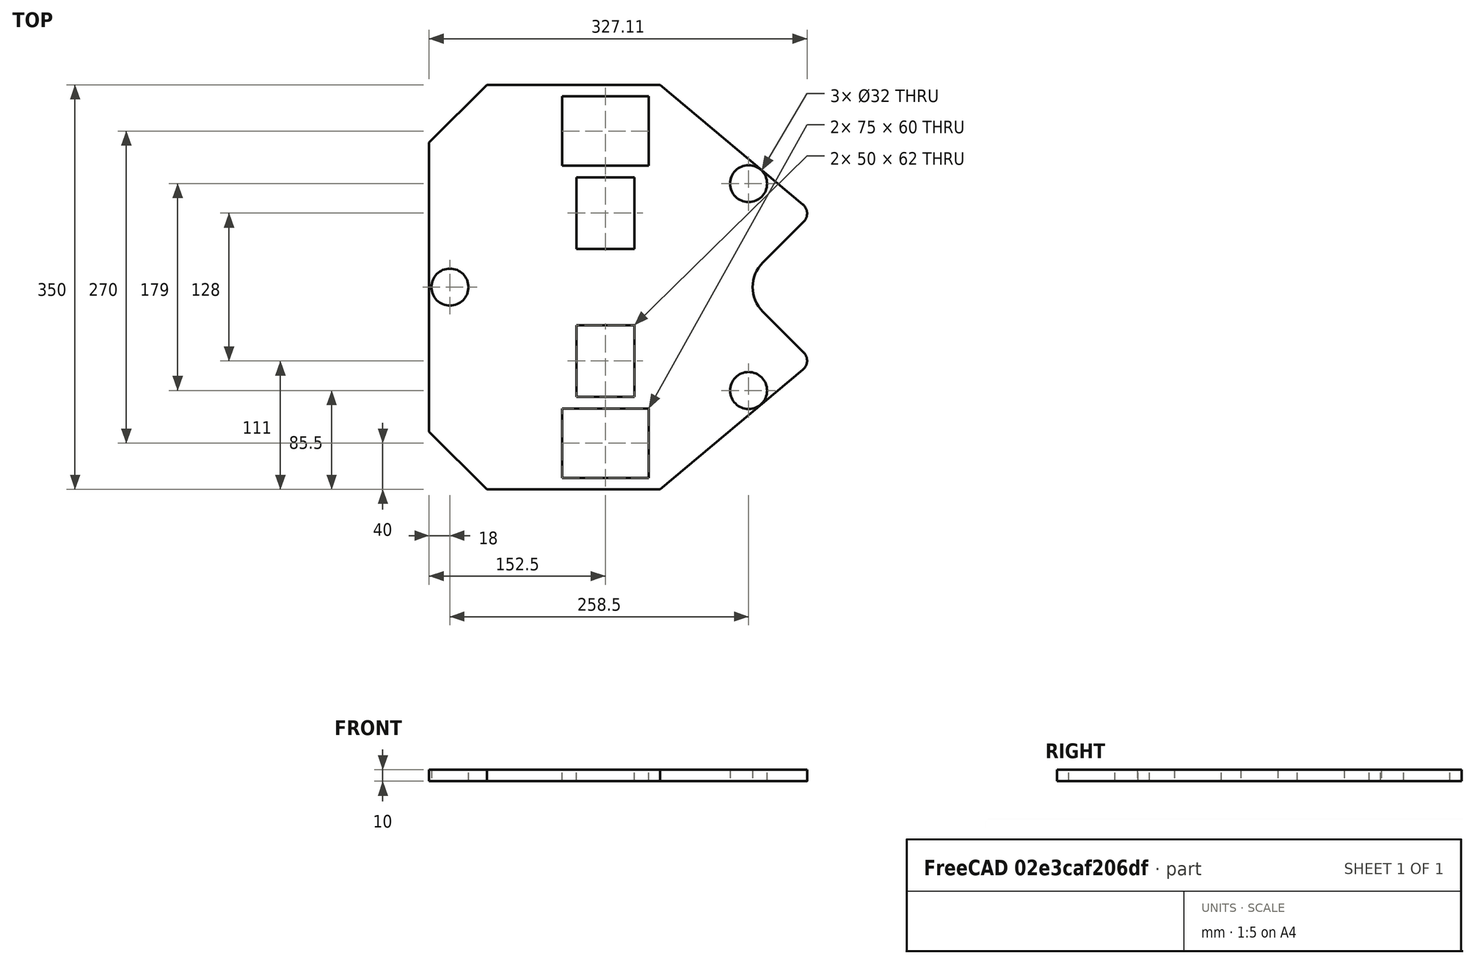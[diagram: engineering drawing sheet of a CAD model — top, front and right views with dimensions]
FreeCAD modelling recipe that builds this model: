
FCSTD DOCUMENT  (FreeCAD 0.15R4669 (Git))
Label: BR_chassis
License: All rights reserved
LicenseURL: http://en.wikipedia.org/wiki/All_rights_reserved
objects: Sketcher::SketchObject×1, Part::Extrusion×1
note: 2 computed .brp shape members not serialized (recipe doc carries the construction recipe); baked Part::Feature solids carry a one-line shape summary decoded from their .brp

FEATURE [Sketcher::SketchObject] Sketch  label="sketchChassis"
  sketch-geometry (31):
    g0: LineSegment StartX=-152.5 StartY=125 StartZ=0 EndX=-152.5 EndY=-125 EndZ=0
    g1: LineSegment StartX=-152.5 StartY=-125 StartZ=0 EndX=-102.5 EndY=-175 EndZ=0
    g2: LineSegment StartX=-102.5 StartY=-175 StartZ=0 EndX=47.5 EndY=-175 EndZ=0
    g3: LineSegment StartX=47.5 StartY=-175 StartZ=0 EndX=171.038 EndY=-71.3392 EndZ=0
    g4: LineSegment StartX=171.038 StartY=71.3392 StartZ=0 EndX=47.5 EndY=175 EndZ=0
    g5: LineSegment StartX=47.5 StartY=175 StartZ=0 EndX=-102.5 EndY=175 EndZ=0
    g6: LineSegment StartX=-102.5 StartY=175 StartZ=0 EndX=-152.5 EndY=125 EndZ=0
    g7: LineSegment StartX=-37.5 StartY=165 StartZ=0 EndX=37.5 EndY=165 EndZ=0
    g8: LineSegment StartX=37.5 StartY=165 StartZ=0 EndX=37.5 EndY=105 EndZ=0
    g9: LineSegment StartX=37.5 StartY=105 StartZ=0 EndX=-37.5 EndY=105 EndZ=0
    g10: LineSegment StartX=-37.5 StartY=105 StartZ=0 EndX=-37.5 EndY=165 EndZ=0
    g11: LineSegment StartX=-37.5 StartY=-105 StartZ=0 EndX=37.5 EndY=-105 EndZ=0
    g12: LineSegment StartX=37.5 StartY=-105 StartZ=0 EndX=37.5 EndY=-165 EndZ=0
    g13: LineSegment StartX=37.5 StartY=-165 StartZ=0 EndX=-37.5 EndY=-165 EndZ=0
    g14: LineSegment StartX=-37.5 StartY=-165 StartZ=0 EndX=-37.5 EndY=-105 EndZ=0
    g15: LineSegment StartX=-25 StartY=33 StartZ=0 EndX=25 EndY=33 EndZ=0
    g16: LineSegment StartX=25 StartY=33 StartZ=0 EndX=25 EndY=95 EndZ=0
    g17: LineSegment StartX=25 StartY=95 StartZ=0 EndX=-25 EndY=95 EndZ=0
    g18: LineSegment StartX=-25 StartY=95 StartZ=0 EndX=-25 EndY=33 EndZ=0
    g19: LineSegment StartX=-25 StartY=-95 StartZ=0 EndX=25 EndY=-95 EndZ=0
    g20: LineSegment StartX=25 StartY=-95 StartZ=0 EndX=25 EndY=-33 EndZ=0
    g21: LineSegment StartX=25 StartY=-33 StartZ=0 EndX=-25 EndY=-33 EndZ=0
    g22: LineSegment StartX=-25 StartY=-33 StartZ=0 EndX=-25 EndY=-95 EndZ=0
    g23: ArcOfCircle CenterX=164.61 CenterY=63.6788 CenterZ=0 NormalX=0 NormalY=0 NormalZ=1 Radius=10 StartAngle=5.49779 EndAngle=7.15585
    g24: ArcOfCircle CenterX=157.5 CenterY=0 CenterZ=0 NormalX=0 NormalY=0 NormalZ=1 Radius=30 StartAngle=2.35619 EndAngle=3.92699
    g25: ArcOfCircle CenterX=164.61 CenterY=-63.6788 CenterZ=0 NormalX=0 NormalY=0 NormalZ=1 Radius=10 StartAngle=5.41052 EndAngle=7.06858
    g26: LineSegment StartX=171.681 StartY=56.6077 StartZ=0 EndX=136.287 EndY=21.2132 EndZ=0
    g27: LineSegment StartX=136.287 StartY=-21.2132 StartZ=0 EndX=171.681 EndY=-56.6077 EndZ=0
    g28: Circle CenterX=124 CenterY=89.5 CenterZ=0 NormalX=0 NormalY=0 NormalZ=1 Radius=16
    g29: Circle CenterX=124 CenterY=-89.5 CenterZ=0 NormalX=0 NormalY=0 NormalZ=1 Radius=16
    g30: Circle CenterX=-134.5 CenterY=0 CenterZ=0 NormalX=0 NormalY=0 NormalZ=1 Radius=16
  constraints (88):
    c: Vertical(g0)
    c: Coincident(g0,g1)
    c: Coincident(g1,g2)
    c: Horizontal(g2)
    c: Coincident(g2,g3)
    c: Coincident(g4,g5)
    c: Horizontal(g5)
    c: Coincident(g5,g6)
    c: Coincident(g6,g0)
    c: Symmetric(g5,g1,g-1)
    c: Symmetric(g0,g0,g-1)
    c: DistanceY(g5,g1) = -350
    c: DistanceX(g0,g5) = 50
    c: DistanceY(g0,g5) = 50
    c: DistanceX(g0,g4) = 200
    c: Symmetric(g4,g3,g-1)
    c: Symmetric(g4,g2,g-1)
    c: Coincident(g7,g8)
    c: Coincident(g8,g9)
    c: Coincident(g9,g10)
    c: Coincident(g10,g7)
    c: Horizontal(g7)
    c: Vertical(g8)
    c: Vertical(g10)
    c: Coincident(g11,g12)
    c: Coincident(g12,g13)
    c: Coincident(g13,g14)
    c: Coincident(g14,g11)
    c: Horizontal(g11)
    c: Horizontal(g13)
    c: Vertical(g12)
    c: Vertical(g14)
    c: Symmetric(g9,g11,g-1)
    c: Symmetric(g13,g7,g-1)
    c: Symmetric(g8,g11,g-1)
    c: DistanceX(g9) = -75
    c: DistanceY(g8) = -60
    c: DistanceY(g4,g7) = -10
    c: Coincident(g15,g16)
    c: Coincident(g16,g17)
    c: Coincident(g17,g18)
    c: Coincident(g18,g15)
    c: Horizontal(g17)
    c: Vertical(g16)
    c: Vertical(g18)
    c: Coincident(g19,g20)
    c: Coincident(g20,g21)
    c: Coincident(g21,g22)
    c: Coincident(g22,g19)
    c: Horizontal(g19)
    c: Horizontal(g21)
    c: Vertical(g20)
    c: Vertical(g22)
    c: Symmetric(g17,g19,g-1)
    c: Symmetric(g21,g15,g-1)
    c: Symmetric(g15,g20,g-1)
    c: DistanceX(g17) = -50
    c: DistanceY(g16) = 62
    c: Symmetric(g9,g8,g-2)
    c: DistanceY(g16,g8) = 10
    c: Symmetric(g15,g15,g-2)
    c: DistanceX(g7,g4) = 10
    c: Angle(g5,g4) = 2.44346
    c: Radius(g24) = 30
    c: Radius(g23) = 10
    c: Coincident(g4,g23)
    c: Coincident(g26,g23)
    c: Coincident(g26,g24)
    c: Coincident(g3,g25)
    c: Coincident(g27,g24)
    c: Coincident(g27,g25)
    c: DistanceX(g4,g24) = 110
    c: Tangent(g24,g26)
    c: PointOnObject(g24,g-1)
    c: Tangent(g26,g23)
    c: Tangent(g23,g4)
    c: Symmetric(g23,g25,g-1)
    c: Symmetric(g24,g24,g-1)
    c: Symmetric(g25,g23,g-1)
    c: Angle(g4,g26) = 1.48353
    c: DistanceX(g-1,g28) = 124
    c: DistanceY(g-1,g28) = 89.5
    c: Radius(g28) = 16
    c: Equal(g29,g28)
    c: Symmetric(g28,g29,g-1)
    c: PointOnObject(g30,g-1)
    c: Equal(g30,g28)
    c: DistanceX(g-1,g30) = -134.5
FEATURE [Part::Extrusion] Extrude  label="plaqueChassis"
  Base = -> Sketch
  Dir = (0,0,10)
  Placement = pos=(0,0,-30) rot=(0,0,1;0rad)
  Solid = true
